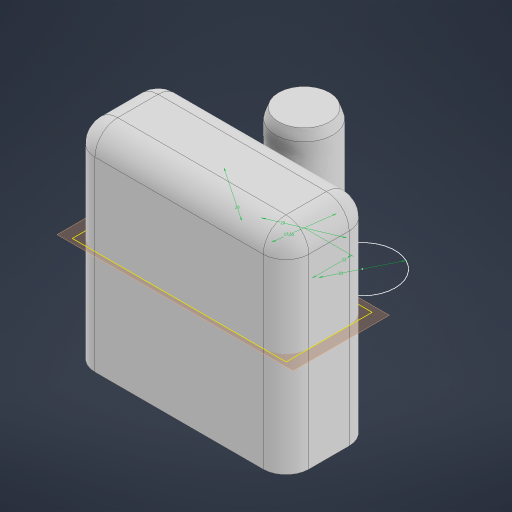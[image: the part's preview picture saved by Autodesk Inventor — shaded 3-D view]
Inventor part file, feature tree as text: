
AUTODESK INVENTOR PART (.ipt)
format: ipt  version: 2023 (Build 270158000, 158)  size: 256,512 bytes
history: native  units: mm
features: extrude x4, sketch x2, fillet x2, chamfer x2, plane x1, projected_geometry x1
ambient origin geometry x8: Origin, YZ Plane, XZ Plane, XY Plane, X Axis, Y Axis, Z Axis, Center Point
bodies: Solid1 (feature_tree)
feature tree (12):
  sketch  "Sketch1"  dims[d0=26.4mm d1=65.7mm]
  extrude  "Extrusion1"  Depth=65.7mm
  extrude  "Extrusion2"  Depth=24.0mm
  fillet  "Fillet1"  Radius=63.3mm
  plane  "Work Plane1"
  sketch  "Sketch3"  dims[d2=1.2mm d3=24.0mm d4=63.3mm d5=1.2mm d6=0.0mm d7=63.0mm d8=0.0mm d9=5.0mm d10=17.65mm d11=20.0mm d12=12.0mm d13=20.0mm d14=20.0mm d15=10.0mm d16=0.0mm d17=64.2mm d18=0.0mm d19=1.0mm d20=3.0mm d21=45.0deg d22=1.0mm d23=3.0mm d24=45.0deg d25=7.0mm d26=0.5mm d27=0.872665mm d28=0.5mm d29=0.872665mm]
  extrude  "Extrusion3"  Depth=1.2mm TaperAngle=0.0deg
  extrude  "Extrusion4"  Depth=63.0mm TaperAngle=0.0deg
  chamfer  "Chamfer1"  Distance=5.0mm
  chamfer  "Chamfer2"  Distance=17.65mm
  fillet  "Fillet2"  Radius=20.0mm
  projected_geometry  "Project Cut Edges1"
